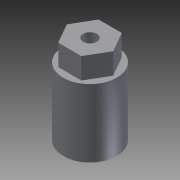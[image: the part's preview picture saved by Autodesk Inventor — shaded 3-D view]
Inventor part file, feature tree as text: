
AUTODESK INVENTOR PART (.ipt)
format: ipt  version: 2012 (Build 160160000, 160)  size: 109,056 bytes
history: native  units: mm
features: extrude x4, sketch x4, chamfer x2, projected_geometry x1
ambient origin geometry x8: Origin, YZ Plane, XZ Plane, XY Plane, X Axis, Y Axis, Z Axis, Center Point
bodies: Solid1 (feature_tree)
feature tree (11):
  extrude  "Extrusion1"  Depth=20.65mm TaperAngle=0.0deg
  chamfer  "Chamfer1"  Distance=0.5mm Angle=45.0deg
  extrude  "Extrusion2"  Depth=12.0mm
  extrude  "Extrusion3"  Depth=6.3mm TaperAngle=0.0deg
  extrude  "Extrusion4"  Depth=20.0mm TaperAngle=0.0deg
  chamfer  "Chamfer3"  Distance=0.5mm Angle=45.0deg
  sketch  "Sketch1"  dims[d0=16.0mm d1=20.65mm d2=0.0mm d3=0.5mm d4=2.0mm d5=45.0deg]
  sketch  "Sketch2"  dims[d7=6.3mm d8=0.0mm d9=12.0mm]
  projected_geometry  "Projected Loop1"
  sketch  "Sketch3"  dims[d10=4.1mm d11=6.3mm d12=0.0mm]
  sketch  "Sketch4"  dims[d16=6.2mm d17=20.0mm d18=0.0mm d19=0.5mm d20=2.0mm d21=45.0deg]
